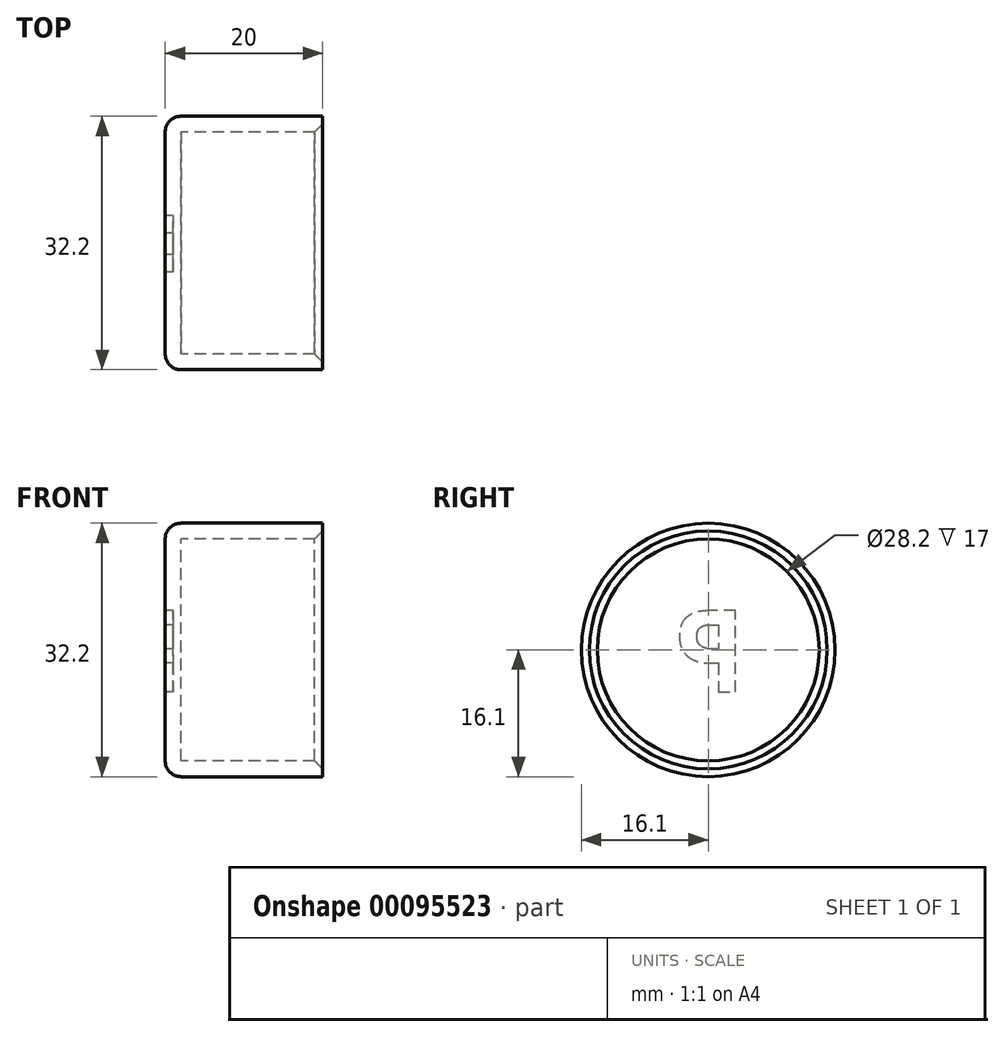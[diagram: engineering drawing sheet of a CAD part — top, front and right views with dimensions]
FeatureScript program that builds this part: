
annotation { "Feature Type Name" : "Feature", "Feature Type Description" : "" }
export const myFeature = defineFeature(function(context is Context, id is Id, definition is map)
    precondition{}
    {
        {
            var Q0;
            Q0=qCreatedBy(makeId("Right.planeOp"),FACE);
            var sketch = newSketch(context, id + "F0", { "sketchPlane" : qUnion([Q0])});
            skCircle(sketch, "E0", {"center": v(0, 0) * mm, "radius": 14.1 * mm});
            skCircle(sketch, "E1.0", {"center": v(0, 0) * mm, "radius": 16.1 * mm});
            skSolve(sketch);
        }
        {
            var Q0;
            Q0=makeQuery(id+"F0.imprint","IMPRINT",FACE,{"disambiguationData":[TD([[makeQuery(id+"F0.imprint","IMPRINT",EDGE,{"derivedFrom":sQuery(id+"F0.wireOp",EDGE,"E0")}),-1.0]])]});
            extrude(context, id + "F1", {"entities" : qUnion([Q0]), "depth" : 20 * mm});
        }
        {
            var Q0;
            Q0=makeQuery(id+"F0.imprint","IMPRINT",FACE,{"disambiguationData":[TD([[makeQuery(id+"F0.imprint","IMPRINT",EDGE,{"derivedFrom":sQuery(id+"F0.wireOp",EDGE,"E0")}),1.0]])]});
            extrude(context, id + "F2", {"entities" : qUnion([Q0]), "operationType" : NewBodyOperationType.ADD, "depth" : 2 * mm});
        }
        {
            var Q0;
            Q0=makeQuery(id+"F1.opExtrude","CAP_EDGE",EDGE,{"disambiguationData":[OSD([sQuery(id+"F0.wireOp",EDGE,"E0")])],"isStart":false});
            chamfer(context, id + "F3", {"entities" : qUnion([Q0]), "width" : 1 * mm, "tangentPropagation" : true});
        }
        {
            var Q0;
            Q0=makeQuery(id+"F1.opExtrude","CAP_EDGE",EDGE,{"disambiguationData":[OSD([sQuery(id+"F0.wireOp",EDGE,"E1.0")])],"isStart":true});
            fillet(context, id + "F4", {"entities" : qUnion([Q0]), "radius" : 2 * mm, "tangentPropagation" : true, "allowEdgeOverflow" : false});
        }
        {
            var Q0;
            {var subQ0=sQuery(id+"F0.wireOp",EDGE,"E0");Q0=makeQuery(id+"F2.boolean.opBoolean","MERGE",FACE,{"derivedFrom":[makeQuery(id+"F1.opExtrude","CAP_FACE",FACE,{"disambiguationData":[OSD([subQ0,sQuery(id+"F0.wireOp",EDGE,"E1.0")])],"isStart":true}),makeQuery(id+"F2.opExtrude","CAP_FACE",FACE,{"disambiguationData":[OSD([subQ0])],"isStart":true})]});}
            var sketch = newSketch(context, id + "F5", { "sketchPlane" : qUnion([Q0])});
            skText(sketch, "E2", { "text": "P", "fontName": "OpenSans-Bold.ttf"});
            const initialGuessF5  = {"E2": [-0.00478, -0.00536, 1, 0, 0.01044]};
            skSetInitialGuess(sketch, initialGuessF5);
            skSolve(sketch);
        }
        {
            var Q0;
            Q0 = qSketchRegion(id + "F5", true);
            extrude(context, id + "F6", {"entities" : qUnion([Q0]), "operationType" : NewBodyOperationType.REMOVE, "oppositeDirection" : true, "depth" : 1 * mm});
        }
    });
